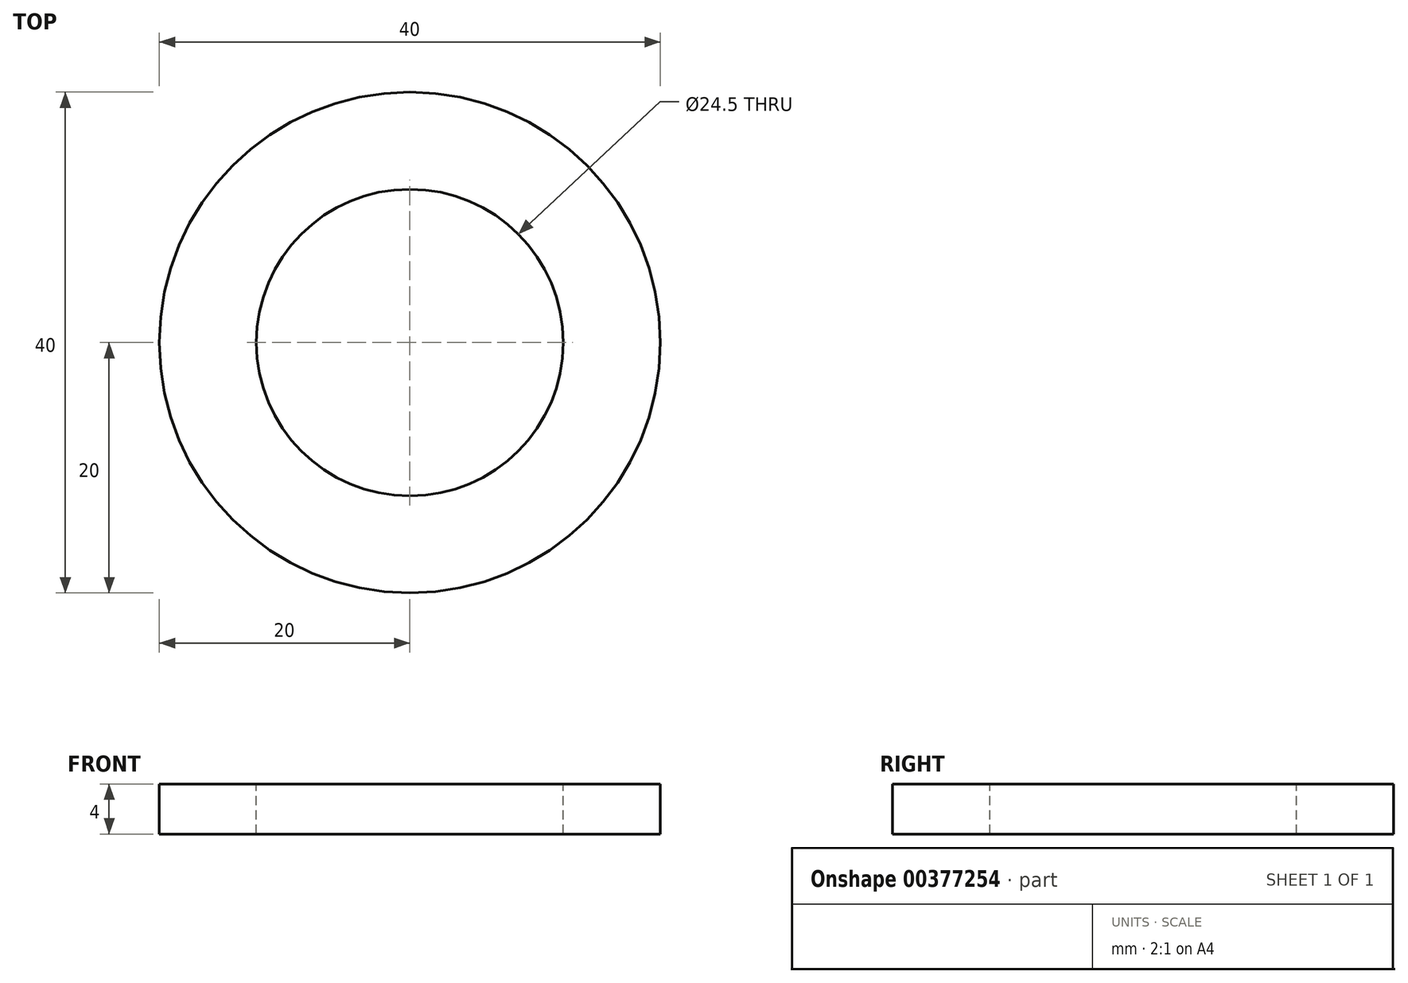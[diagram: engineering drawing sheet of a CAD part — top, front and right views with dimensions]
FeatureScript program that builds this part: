
annotation { "Feature Type Name" : "Feature", "Feature Type Description" : "" }
export const myFeature = defineFeature(function(context is Context, id is Id, definition is map)
    precondition{}
    {
        {
            var Q0;
            Q0=qCreatedBy(makeId("Top.planeOp"),FACE);
            var sketch = newSketch(context, id + "F0", { "sketchPlane" : qUnion([Q0])});
            skCircle(sketch, "E0", {"center": v(0, 0) * mm, "radius": 20 * mm});
            skSolve(sketch);
        }
        {
            var Q0;
            Q0=makeQuery(id+"F0.imprint","IMPRINT",FACE,{"disambiguationData":[TD([[makeQuery(id+"F0.imprint","IMPRINT",EDGE,{"derivedFrom":sQuery(id+"F0.wireOp",EDGE,"E0")}),1.0]])]});
            extrude(context, id + "F1", {"entities" : qUnion([Q0]), "depth" : 4 * mm});
        }
        {
            var Q0;
            Q0=makeQuery(id+"F1.opExtrude","CAP_FACE",FACE,{"disambiguationData":[OSD([sQuery(id+"F0.wireOp",EDGE,"E0")])],"isStart":false});
            var sketch = newSketch(context, id + "F2", { "sketchPlane" : qUnion([Q0])});
            skPoint(sketch, "E1", {"position": v(0, 0) * mm});
            skSolve(sketch);
        }
        {
            var Q0;
            Q0=sQuery(id+"F2.wireOp",VERTEX,"E1");
            var Q1;
            Q1=makeQuery(id+"F1.opExtrude","SWEPT_BODY",BODY,{"disambiguationData":[OSD([sQuery(id+"F0.wireOp",EDGE,"E0")])]});
            hole(context, id + "F3", {"style" : HoleStyle.SIMPLE, "endStyle" : HoleEndStyle.THROUGH, "standardTappedOrClearance" : lookupTablePath({ "standard" : "ISO", "size" : "24.5", "type" : "Drilled" }), "standardBlindInLast" : lookupTablePath({ "standard" : "ISO", "size" : "24.5", "type" : "Drilled" }), "holeDiameter" : 24.5 * mm, "isTappedThrough" : true, "tappedDepth" : 12 * mm, "tapClearance" : 3, "locations" : qUnion([Q0]), "scope" : qUnion([Q1])});
        }
    });
